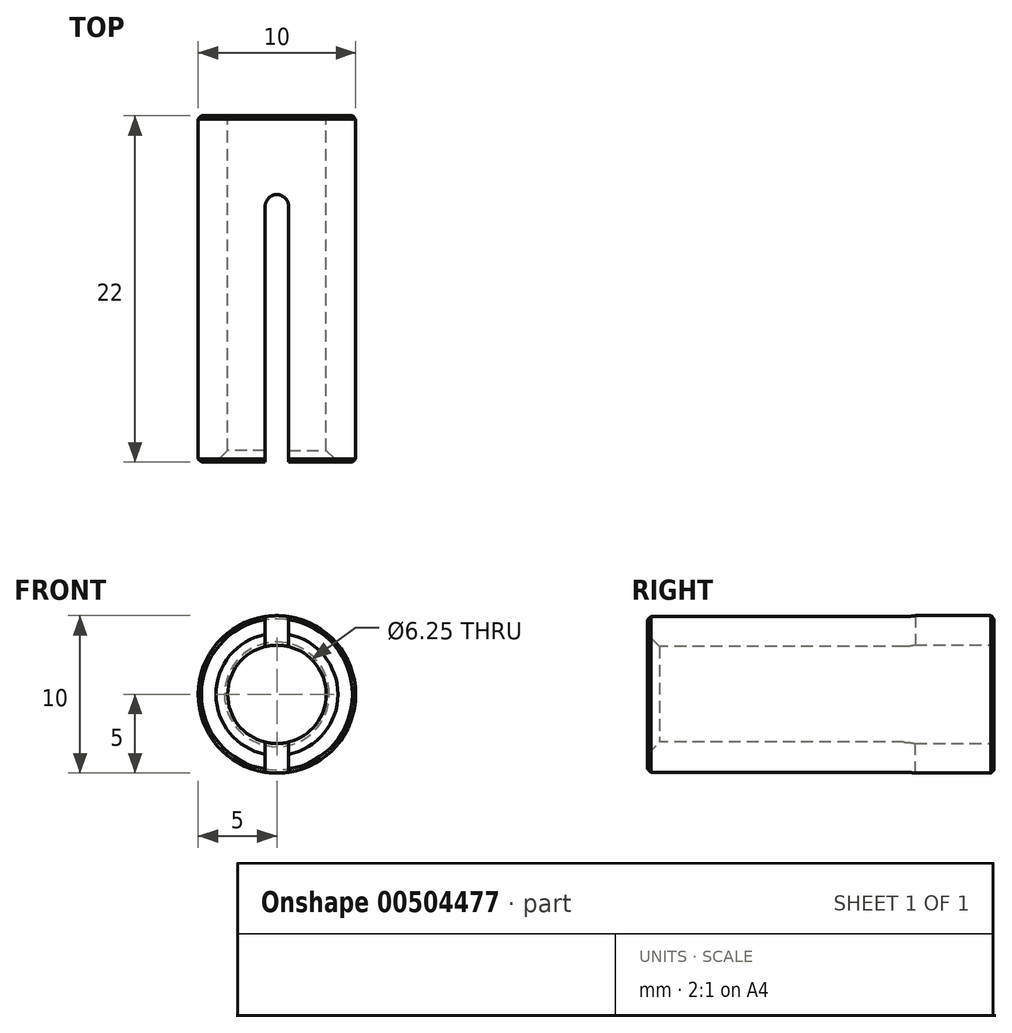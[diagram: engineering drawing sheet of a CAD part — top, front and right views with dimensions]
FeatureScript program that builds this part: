
annotation { "Feature Type Name" : "Feature", "Feature Type Description" : "" }
export const myFeature = defineFeature(function(context is Context, id is Id, definition is map)
    precondition{}
    {
        {
            var Q0;
            Q0=qCreatedBy(makeId("Front.planeOp"),FACE);
            var sketch = newSketch(context, id + "F0", { "sketchPlane" : qUnion([Q0])});
            skCircle(sketch, "E0", {"center": v(0, 0) * mm, "radius": 5 * mm});
            skCircle(sketch, "E1", {"center": v(0, 0) * mm, "radius": 3.12 * mm});
            skSolve(sketch);
        }
        {
            var Q0;
            Q0=makeQuery(id+"F0.imprint","IMPRINT",FACE,{"disambiguationData":[TD([[makeQuery(id+"F0.imprint","IMPRINT",EDGE,{"derivedFrom":sQuery(id+"F0.wireOp",EDGE,"E0")}),1.0]])]});
            extrude(context, id + "F1", {"entities" : qUnion([Q0]), "depth" : 22 * mm});
        }
        {
            var Q0;
            Q0=makeQuery(id+"F1.opExtrude","CAP_FACE",FACE,{"disambiguationData":[OSD([sQuery(id+"F0.wireOp",EDGE,"E0"),sQuery(id+"F0.wireOp",EDGE,"E1")])],"isStart":false});
            var sketch = newSketch(context, id + "F2", { "sketchPlane" : qUnion([Q0])});
            skLineSegment(sketch, "E2.bottom", {"start": v(0.75, -5.66) * mm, "end": v(-0.75, -5.66) * mm});
            skLineSegment(sketch, "E2.top", {"start": v(0.75, 5.66) * mm, "end": v(-0.75, 5.66) * mm});
            skLineSegment(sketch, "E2.left", {"start": v(0.75, -5.66) * mm, "end": v(0.75, 5.66) * mm});
            skLineSegment(sketch, "E2.right", {"start": v(-0.75, -5.66) * mm, "end": v(-0.75, 5.66) * mm});
            skPoint(sketch, "E2.middle", {"position": v(0, 0) * mm});
            skSolve(sketch);
        }
        {
            var Q0;
            {var subQ0=sQuery(id+"F2.wireOp",EDGE,"E2.left");var subQ1=makeQuery(id+"F1.opExtrude","CAP_EDGE",EDGE,{"disambiguationData":[OSD([sQuery(id+"F0.wireOp",EDGE,"E0")])],"isStart":false});var subQ2=makeQuery(id+"F2.imprint","INTERSECT",VERTEX,{"disambiguationData":[OD(1.0)],"derivedFrom":[subQ1,subQ0]});Q0=makeQuery(id+"F2.imprint","IMPRINT",FACE,{"disambiguationData":[TD([[makeQuery(id+"F2.imprint","IMPRINT",EDGE,{"disambiguationData":[TD([[subQ2,1.0]])],"derivedFrom":subQ0}),1.0]])]});}
            var Q1;
            {var subQ0=sQuery(id+"F2.wireOp",EDGE,"E2.left");var subQ1=makeQuery(id+"F1.opExtrude","CAP_EDGE",EDGE,{"disambiguationData":[OSD([sQuery(id+"F0.wireOp",EDGE,"E0")])],"isStart":false});var subQ2=makeQuery(id+"F2.imprint","INTERSECT",VERTEX,{"disambiguationData":[OD(0.0)],"derivedFrom":[subQ1,subQ0]});Q1=makeQuery(id+"F2.imprint","IMPRINT",FACE,{"disambiguationData":[TD([[makeQuery(id+"F2.imprint","IMPRINT",EDGE,{"disambiguationData":[TD([[subQ2,-1.0]])],"derivedFrom":subQ0}),1.0]])]});}
            extrude(context, id + "F3", {"entities" : qUnion([Q0, Q1]), "operationType" : NewBodyOperationType.REMOVE, "oppositeDirection" : true, "depth" : 17 * mm});
        }
        {
            var Q0;
            Q0=makeQuery(id+"F1.opExtrude","CAP_EDGE",EDGE,{"disambiguationData":[OSD([sQuery(id+"F0.wireOp",EDGE,"E0")])],"isStart":true});
            var Q1;
            {var subQ0=sQuery(id+"F0.wireOp",EDGE,"E0");var subQ1=sQuery(id+"F2.wireOp",EDGE,"E2.right");var subQ2=makeQuery(id+"F1.opExtrude","CAP_EDGE",EDGE,{"disambiguationData":[OSD([subQ0])],"isStart":false});Q1=makeQuery(id+"F3.boolean.opBoolean","SPLIT",EDGE,{"disambiguationData":[TD([makeQuery(id+"F3.opExtrude","SWEPT_FACE",FACE,{"disambiguationData":[OSD([subQ1]),TDD([makeQuery(id+"F2.imprint","IMPRINT",EDGE,{"disambiguationData":[TD([[makeQuery(id+"F2.imprint","INTERSECT",VERTEX,{"disambiguationData":[OD(0.0)],"derivedFrom":[subQ2,subQ1]}),-1.0]])],"derivedFrom":subQ1})])]})])],"derivedFrom":subQ2});}
            var Q2;
            {var subQ0=sQuery(id+"F0.wireOp",EDGE,"E0");var subQ2=sQuery(id+"F2.wireOp",EDGE,"E2.left");var subQ3=makeQuery(id+"F1.opExtrude","CAP_EDGE",EDGE,{"disambiguationData":[OSD([subQ0])],"isStart":false});Q2=makeQuery(id+"F3.boolean.opBoolean","SPLIT",EDGE,{"disambiguationData":[TD([makeQuery(id+"F3.opExtrude","SWEPT_FACE",FACE,{"disambiguationData":[OSD([subQ2]),TDD([makeQuery(id+"F2.imprint","IMPRINT",EDGE,{"disambiguationData":[TD([[makeQuery(id+"F2.imprint","INTERSECT",VERTEX,{"disambiguationData":[OD(0.0)],"derivedFrom":[subQ3,subQ2]}),-1.0]])],"derivedFrom":subQ2})])]})])],"derivedFrom":subQ3});}
            var Q3;
            Q3=makeQuery(id+"F1.opExtrude","CAP_EDGE",EDGE,{"disambiguationData":[OSD([sQuery(id+"F0.wireOp",EDGE,"E1")])],"isStart":true});
            chamfer(context, id + "F4", {"entities" : qUnion([Q0, Q1, Q2, Q3]), "width" : 0.2 * mm, "tangentPropagation" : true});
        }
        {
            var Q0;
            {var subQ0=sQuery(id+"F0.wireOp",EDGE,"E1");var subQ1=sQuery(id+"F0.wireOp",EDGE,"E0");var subQ2=sQuery(id+"F2.wireOp",EDGE,"E2.right");var subQ3=makeQuery(id+"F1.opExtrude","CAP_EDGE",EDGE,{"disambiguationData":[OSD([subQ1])],"isStart":false});var subQ4=makeQuery(id+"F1.opExtrude","CAP_EDGE",EDGE,{"disambiguationData":[OSD([subQ0])],"isStart":false});Q0=makeQuery(id+"F3.boolean.opBoolean","SPLIT",EDGE,{"disambiguationData":[TD([makeQuery(id+"F3.opExtrude","SWEPT_FACE",FACE,{"disambiguationData":[OSD([subQ2]),TDD([makeQuery(id+"F2.imprint","IMPRINT",EDGE,{"disambiguationData":[TD([[makeQuery(id+"F2.imprint","INTERSECT",VERTEX,{"disambiguationData":[OD(0.0)],"derivedFrom":[subQ3,subQ2]}),-1.0]])],"derivedFrom":subQ2})])]})])],"derivedFrom":subQ4});}
            var Q1;
            {var subQ0=sQuery(id+"F0.wireOp",EDGE,"E1");var subQ1=sQuery(id+"F0.wireOp",EDGE,"E0");var subQ2=sQuery(id+"F2.wireOp",EDGE,"E2.left");var subQ3=makeQuery(id+"F1.opExtrude","CAP_EDGE",EDGE,{"disambiguationData":[OSD([subQ1])],"isStart":false});var subQ4=makeQuery(id+"F1.opExtrude","CAP_EDGE",EDGE,{"disambiguationData":[OSD([subQ0])],"isStart":false});Q1=makeQuery(id+"F3.boolean.opBoolean","SPLIT",EDGE,{"disambiguationData":[TD([makeQuery(id+"F3.opExtrude","SWEPT_FACE",FACE,{"disambiguationData":[OSD([subQ2]),TDD([makeQuery(id+"F2.imprint","IMPRINT",EDGE,{"disambiguationData":[TD([[makeQuery(id+"F2.imprint","INTERSECT",VERTEX,{"disambiguationData":[OD(0.0)],"derivedFrom":[subQ3,subQ2]}),-1.0]])],"derivedFrom":subQ2})])]})])],"derivedFrom":subQ4});}
            chamfer(context, id + "F5", {"entities" : qUnion([Q0, Q1]), "width" : 0.75 * mm, "tangentPropagation" : true});
        }
        {
            var Q0;
            {var subQ0=sQuery(id+"F2.wireOp",EDGE,"E2.left");Q0=makeQuery(id+"F3.boolean.opBoolean","COPY",EDGE,{"derivedFrom":makeQuery(id+"F3.opExtrude","CAP_EDGE",EDGE,{"disambiguationData":[OSD([subQ0]),TDD([makeQuery(id+"F2.imprint","IMPRINT",EDGE,{"disambiguationData":[TD([[makeQuery(id+"F2.imprint","INTERSECT",VERTEX,{"disambiguationData":[OD(0.0)],"derivedFrom":[makeQuery(id+"F1.opExtrude","CAP_EDGE",EDGE,{"disambiguationData":[OSD([sQuery(id+"F0.wireOp",EDGE,"E0")])],"isStart":false}),subQ0]}),-1.0]])],"derivedFrom":subQ0})])],"isStart":false})});}
            var Q1;
            {var subQ0=sQuery(id+"F2.wireOp",EDGE,"E2.right");Q1=makeQuery(id+"F3.boolean.opBoolean","COPY",EDGE,{"derivedFrom":makeQuery(id+"F3.opExtrude","CAP_EDGE",EDGE,{"disambiguationData":[OSD([subQ0]),TDD([makeQuery(id+"F2.imprint","IMPRINT",EDGE,{"disambiguationData":[TD([[makeQuery(id+"F2.imprint","INTERSECT",VERTEX,{"disambiguationData":[OD(0.0)],"derivedFrom":[makeQuery(id+"F1.opExtrude","CAP_EDGE",EDGE,{"disambiguationData":[OSD([sQuery(id+"F0.wireOp",EDGE,"E0")])],"isStart":false}),subQ0]}),-1.0]])],"derivedFrom":subQ0})])],"isStart":false})});}
            var Q2;
            {var subQ0=sQuery(id+"F2.wireOp",EDGE,"E2.right");Q2=makeQuery(id+"F3.boolean.opBoolean","COPY",EDGE,{"derivedFrom":makeQuery(id+"F3.opExtrude","CAP_EDGE",EDGE,{"disambiguationData":[OSD([subQ0]),TDD([makeQuery(id+"F2.imprint","IMPRINT",EDGE,{"disambiguationData":[TD([[makeQuery(id+"F2.imprint","INTERSECT",VERTEX,{"disambiguationData":[OD(1.0)],"derivedFrom":[makeQuery(id+"F1.opExtrude","CAP_EDGE",EDGE,{"disambiguationData":[OSD([sQuery(id+"F0.wireOp",EDGE,"E0")])],"isStart":false}),subQ0]}),1.0]])],"derivedFrom":subQ0})])],"isStart":false})});}
            var Q3;
            {var subQ0=sQuery(id+"F2.wireOp",EDGE,"E2.left");Q3=makeQuery(id+"F3.boolean.opBoolean","COPY",EDGE,{"derivedFrom":makeQuery(id+"F3.opExtrude","CAP_EDGE",EDGE,{"disambiguationData":[OSD([subQ0]),TDD([makeQuery(id+"F2.imprint","IMPRINT",EDGE,{"disambiguationData":[TD([[makeQuery(id+"F2.imprint","INTERSECT",VERTEX,{"disambiguationData":[OD(1.0)],"derivedFrom":[makeQuery(id+"F1.opExtrude","CAP_EDGE",EDGE,{"disambiguationData":[OSD([sQuery(id+"F0.wireOp",EDGE,"E0")])],"isStart":false}),subQ0]}),1.0]])],"derivedFrom":subQ0})])],"isStart":false})});}
            fillet(context, id + "F6", {"entities" : qUnion([Q0, Q1, Q2, Q3]), "radius" : (1.5 / 2) * mm, "tangentPropagation" : true, "allowEdgeOverflow" : false});
        }
    });
